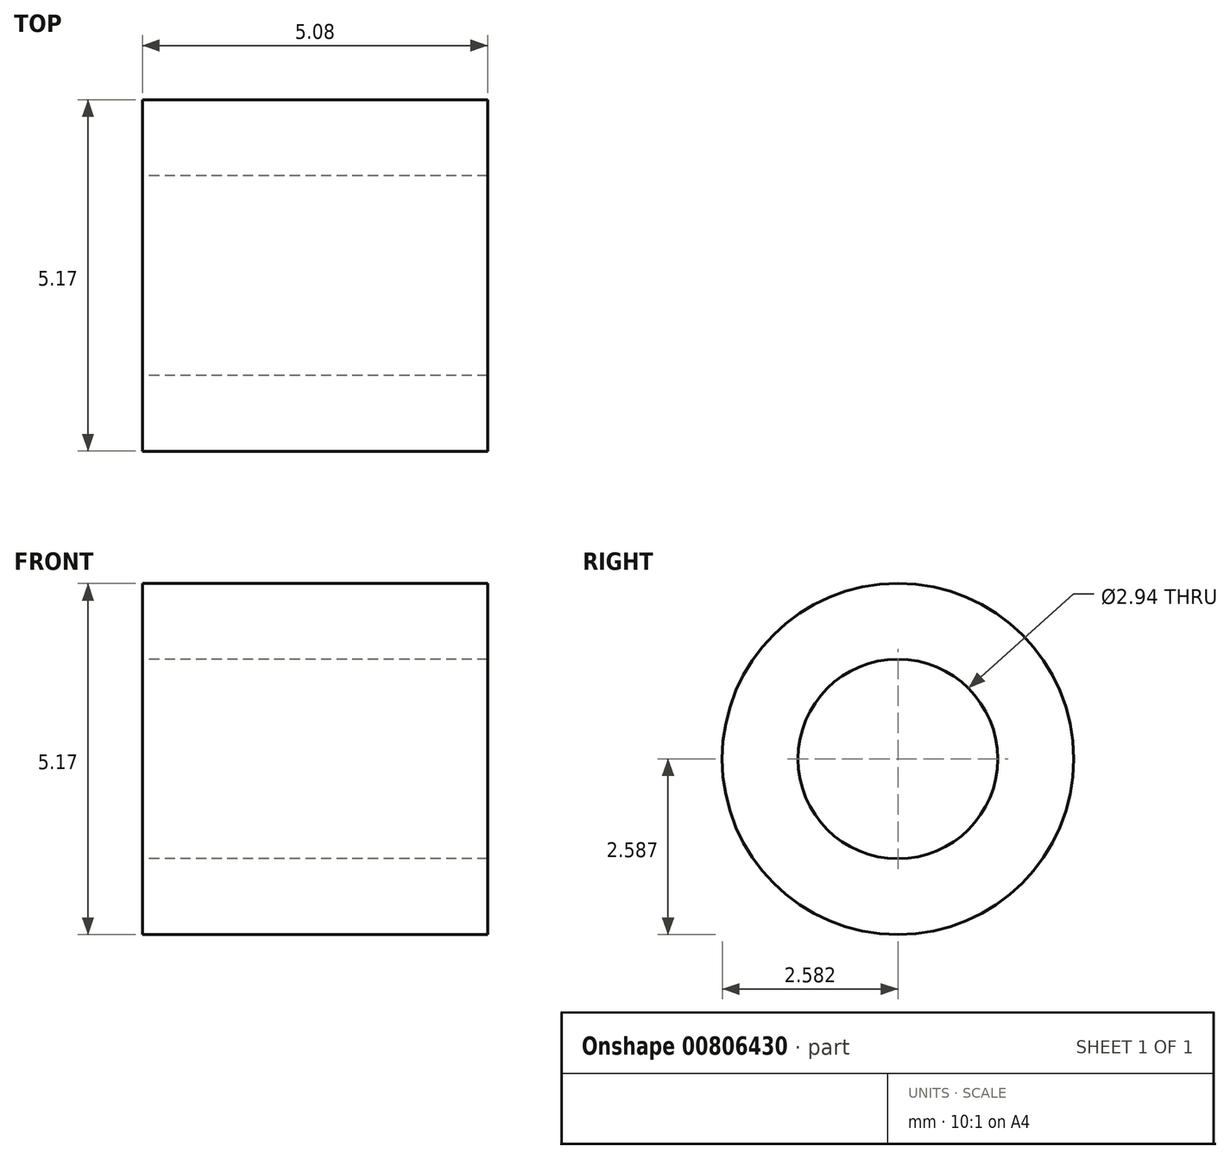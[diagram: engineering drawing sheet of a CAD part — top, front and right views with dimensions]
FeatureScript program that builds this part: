
annotation { "Feature Type Name" : "Feature", "Feature Type Description" : "" }
export const myFeature = defineFeature(function(context is Context, id is Id, definition is map)
    precondition{}
    {
        {
            var Q0;
            Q0=qCreatedBy(makeId("Right.planeOp"),FACE);
            var sketch = newSketch(context, id + "F0", { "sketchPlane" : qUnion([Q0])});
            skCircle(sketch, "E0", {"center": v(18.98, 47.93) * mm, "radius": 2.59 * mm});
            skPoint(sketch, "E0.first.point", {"position": v(21.52, 47.44) * mm});
            skPoint(sketch, "E0.second.point", {"position": v(17.2, 46.06) * mm});
            skPoint(sketch, "E0.third.point", {"position": v(16.43, 48.35) * mm});
            skCircle(sketch, "E1", {"center": v(18.98, 47.93) * mm, "radius": 1.47 * mm});
            skPoint(sketch, "E1.first.point", {"position": v(20.3, 48.6) * mm});
            skPoint(sketch, "E1.second.point", {"position": v(17.71, 47.19) * mm});
            skPoint(sketch, "E1.third.point", {"position": v(18.98, 46.46) * mm});
            skSolve(sketch);
        }
        {
            var Q0;
            Q0=makeQuery(id+"F0.imprint","IMPRINT",FACE,{"disambiguationData":[TD([[makeQuery(id+"F0.imprint","IMPRINT",EDGE,{"derivedFrom":sQuery(id+"F0.wireOp",EDGE,"E0")}),1.0]])]});
            extrude(context, id + "F1", {"entities" : qUnion([Q0]), "endBound" : BoundingType.SYMMETRIC, "depth" : 5.08 * mm, "offsetDistance" : 25.4 * mm});
        }
    });
